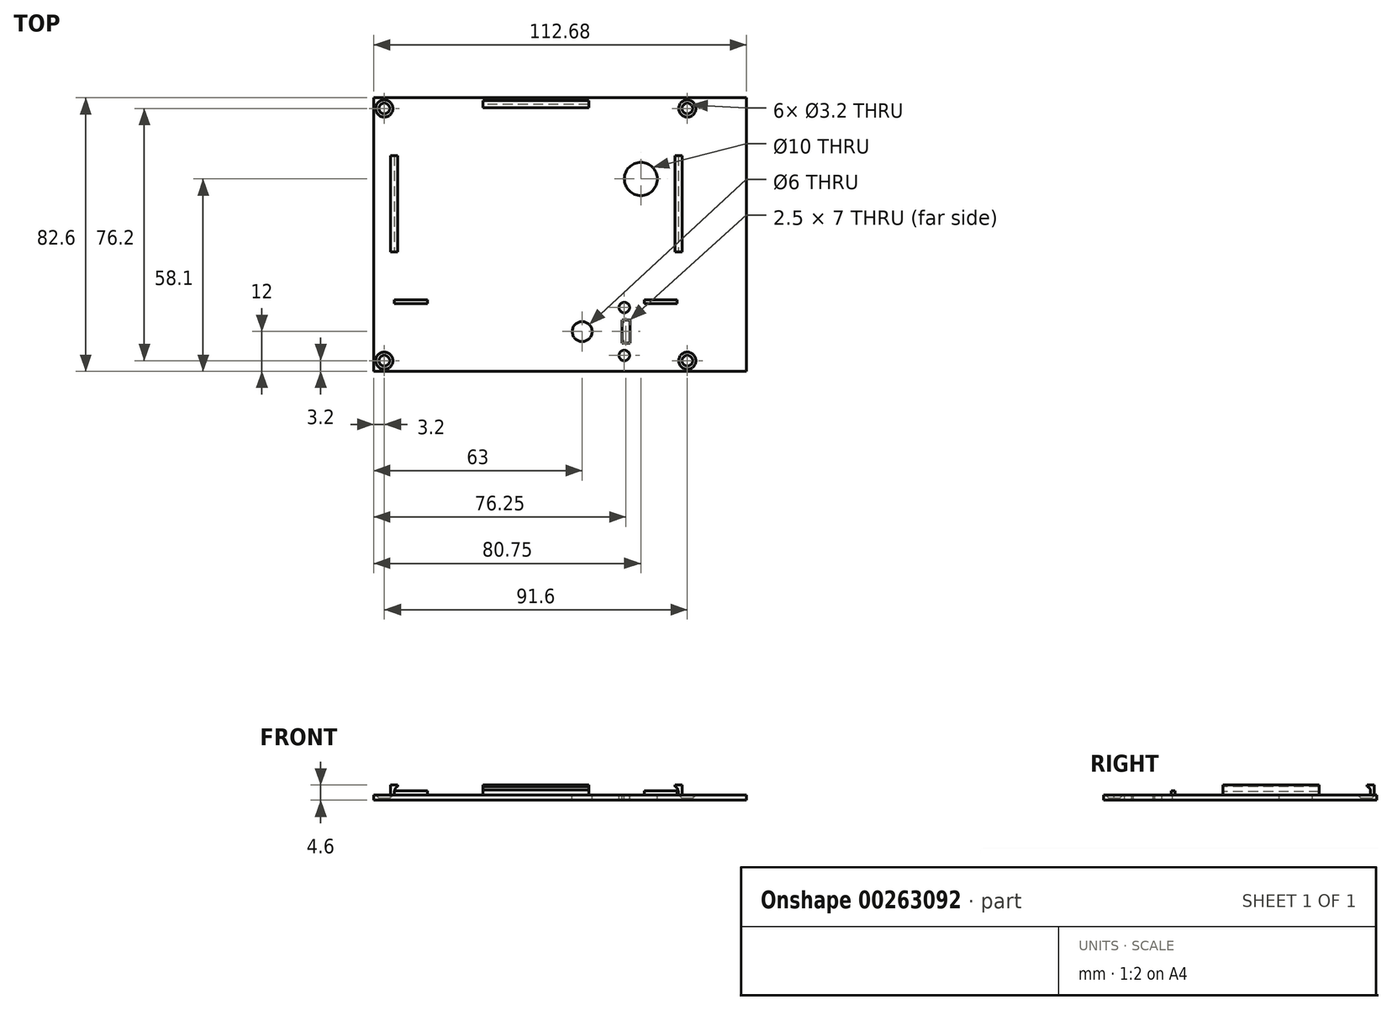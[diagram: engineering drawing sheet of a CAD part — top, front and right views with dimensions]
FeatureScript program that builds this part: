
annotation { "Feature Type Name" : "Feature", "Feature Type Description" : "" }
export const myFeature = defineFeature(function(context is Context, id is Id, definition is map)
    precondition{}
    {
        {
            var Q0;
            Q0=qCreatedBy(makeId("Top.planeOp"),FACE);
            var sketch = newSketch(context, id + "F0", { "sketchPlane" : qUnion([Q0])});
            skLineSegment(sketch, "E0.bottom", {"start": v(0, 0) * mm, "end": v(112.68, 0) * mm});
            skLineSegment(sketch, "E0.top", {"start": v(0, 82.6) * mm, "end": v(112.68, 82.6) * mm});
            skLineSegment(sketch, "E0.left", {"start": v(0, 0) * mm, "end": v(0, 82.6) * mm});
            skLineSegment(sketch, "E0.right", {"start": v(112.68, 0) * mm, "end": v(112.68, 82.6) * mm});
            skLineSegment(sketch, "E1.bottom", {"start": v(3.2, 79.4) * mm, "end": v(94.8, 79.4) * mm, "construction": true});
            skLineSegment(sketch, "E1.top", {"start": v(3.2, 3.2) * mm, "end": v(94.8, 3.2) * mm, "construction": true});
            skLineSegment(sketch, "E1.left", {"start": v(3.2, 79.4) * mm, "end": v(3.2, 3.2) * mm, "construction": true});
            skLineSegment(sketch, "E1.right", {"start": v(94.8, 79.4) * mm, "end": v(94.8, 3.2) * mm, "construction": true});
            skCircle(sketch, "E2", {"center": v(3.2, 79.4) * mm, "radius": 1.6 * mm});
            skCircle(sketch, "E3", {"center": v(94.8, 79.4) * mm, "radius": 1.6 * mm});
            skCircle(sketch, "E4", {"center": v(94.8, 3.2) * mm, "radius": 1.6 * mm});
            skCircle(sketch, "E5", {"center": v(3.2, 3.2) * mm, "radius": 1.6 * mm});
            skSolve(sketch);
        }
        {
            var Q0;
            Q0=makeQuery(id+"F0.imprint","IMPRINT",FACE,{"disambiguationData":[TD([[makeQuery(id+"F0.imprint","IMPRINT",EDGE,{"derivedFrom":sQuery(id+"F0.wireOp",EDGE,"E0.bottom")}),1.0]])]});
            var sketch = newSketch(context, id + "F1", { "sketchPlane" : qUnion([Q0])});
            skLineSegment(sketch, "E6.bottom", {"start": v(6.25, 80.6) * mm, "end": v(91.75, 80.6) * mm, "construction": true});
            skLineSegment(sketch, "E6.top", {"start": v(6.25, 21.6) * mm, "end": v(91.75, 21.6) * mm, "construction": true});
            skLineSegment(sketch, "E6.left", {"start": v(6.25, 80.6) * mm, "end": v(6.25, 21.6) * mm, "construction": true});
            skLineSegment(sketch, "E6.right", {"start": v(91.75, 80.6) * mm, "end": v(91.75, 21.6) * mm, "construction": true});
            skCircle(sketch, "E7", {"center": v(80.75, 58.1) * mm, "radius": 5 * mm});
            skLineSegment(sketch, "E8", {"start": v(49, 80.6) * mm, "end": v(49, 21.6) * mm, "construction": true});
            skLineSegment(sketch, "E9.bottom", {"start": v(6.25, 21.6) * mm, "end": v(16.25, 21.6) * mm});
            skLineSegment(sketch, "E9.top", {"start": v(6.25, 20.4) * mm, "end": v(16.25, 20.4) * mm});
            skLineSegment(sketch, "E9.left", {"start": v(6.25, 21.6) * mm, "end": v(6.25, 20.4) * mm});
            skLineSegment(sketch, "E9.right", {"start": v(16.25, 21.6) * mm, "end": v(16.25, 20.4) * mm});
            skLineSegment(sketch, "E10.bottom", {"start": v(91.75, 21.6) * mm, "end": v(81.75, 21.6) * mm});
            skLineSegment(sketch, "E10.top", {"start": v(91.75, 20.4) * mm, "end": v(81.75, 20.4) * mm});
            skLineSegment(sketch, "E10.left", {"start": v(91.75, 21.6) * mm, "end": v(91.75, 20.4) * mm});
            skLineSegment(sketch, "E10.right", {"start": v(81.75, 21.6) * mm, "end": v(81.75, 20.4) * mm});
            skSolve(sketch);
        }
        {
            var Q0;
            Q0=makeQuery(id+"F0.imprint","IMPRINT",FACE,{"disambiguationData":[TD([[makeQuery(id+"F0.imprint","IMPRINT",EDGE,{"derivedFrom":sQuery(id+"F0.wireOp",EDGE,"E0.bottom")}),1.0]])]});
            var sketch = newSketch(context, id + "F2", { "sketchPlane" : qUnion([Q0])});
            skLineSegment(sketch, "E11.bottom", {"start": v(53.5, 22.5) * mm, "end": v(82.5, 22.5) * mm, "construction": true});
            skLineSegment(sketch, "E11.top", {"start": v(53.5, 1.5) * mm, "end": v(82.5, 1.5) * mm, "construction": true});
            skLineSegment(sketch, "E11.left", {"start": v(53.5, 22.5) * mm, "end": v(53.5, 1.5) * mm, "construction": true});
            skLineSegment(sketch, "E11.right", {"start": v(82.5, 22.5) * mm, "end": v(82.5, 1.5) * mm, "construction": true});
            skCircle(sketch, "E12", {"center": v(75.75, 19.25) * mm, "radius": 1.6 * mm});
            skCircle(sketch, "E13", {"center": v(75.75, 4.75) * mm, "radius": 1.6 * mm});
            skCircle(sketch, "E14", {"center": v(63, 12) * mm, "radius": 3 * mm});
            skLineSegment(sketch, "E15.bottom", {"start": v(75, 15.5) * mm, "end": v(77.5, 15.5) * mm});
            skLineSegment(sketch, "E15.top", {"start": v(75, 8.5) * mm, "end": v(77.5, 8.5) * mm});
            skLineSegment(sketch, "E15.left", {"start": v(75, 15.5) * mm, "end": v(75, 8.5) * mm});
            skLineSegment(sketch, "E15.right", {"start": v(77.5, 15.5) * mm, "end": v(77.5, 8.5) * mm});
            skSolve(sketch);
        }
        {
            var Q0;
            Q0=makeQuery(id+"F0.imprint","IMPRINT",FACE,{"disambiguationData":[TD([[makeQuery(id+"F0.imprint","IMPRINT",EDGE,{"derivedFrom":sQuery(id+"F0.wireOp",EDGE,"E0.bottom")}),1.0]])]});
            extrude(context, id + "F3", {"entities" : qUnion([Q0]), "oppositeDirection" : true, "depth" : 1.6 * mm});
        }
        {
            var Q0;
            Q0=makeQuery(id+"F1.imprint","IMPRINT",FACE,{"disambiguationData":[TD([[makeQuery(id+"F1.imprint","IMPRINT",EDGE,{"derivedFrom":sQuery(id+"F1.wireOp",EDGE,"E7")}),1.0]])]});
            extrude(context, id + "F4", {"entities" : qUnion([Q0]), "operationType" : NewBodyOperationType.REMOVE, "endBound" : BoundingType.THROUGH_ALL, "oppositeDirection" : true, "depth" : 25 * mm});
        }
        {
            var Q0;
            Q0=makeQuery(id+"F2.imprint","IMPRINT",FACE,{"disambiguationData":[TD([[makeQuery(id+"F2.imprint","IMPRINT",EDGE,{"derivedFrom":sQuery(id+"F2.wireOp",EDGE,"E13")}),1.0]])]});
            var Q1;
            Q1=makeQuery(id+"F2.imprint","IMPRINT",FACE,{"disambiguationData":[TD([[makeQuery(id+"F2.imprint","IMPRINT",EDGE,{"derivedFrom":sQuery(id+"F2.wireOp",EDGE,"E14")}),1.0]])]});
            var Q2;
            Q2=makeQuery(id+"F2.imprint","IMPRINT",FACE,{"disambiguationData":[TD([[makeQuery(id+"F2.imprint","IMPRINT",EDGE,{"derivedFrom":sQuery(id+"F2.wireOp",EDGE,"E15.bottom")}),-1.0]])]});
            var Q3;
            Q3=makeQuery(id+"F2.imprint","IMPRINT",FACE,{"disambiguationData":[TD([[makeQuery(id+"F2.imprint","IMPRINT",EDGE,{"derivedFrom":sQuery(id+"F2.wireOp",EDGE,"E12")}),1.0]])]});
            extrude(context, id + "F5", {"entities" : qUnion([Q0, Q1, Q2, Q3]), "operationType" : NewBodyOperationType.REMOVE, "endBound" : BoundingType.THROUGH_ALL, "oppositeDirection" : true, "depth" : 25 * mm});
        }
        {
            var Q0;
            Q0=qCreatedBy(makeId("Front.planeOp"),FACE);
            var sketch = newSketch(context, id + "F6", { "sketchPlane" : qUnion([Q0])});
            skLineSegment(sketch, "E16", {"start": v(6.25, 0) * mm, "end": v(5.05, 0) * mm});
            skLineSegment(sketch, "E17.bottom", {"start": v(5.05, 0) * mm, "end": v(6.25, 0) * mm});
            skLineSegment(sketch, "E17.top", {"start": v(5.05, 0) * mm, "end": v(6.25, 0) * mm});
            skLineSegment(sketch, "E17.left", {"start": v(5.05, 0) * mm, "end": v(5.05, 0) * mm});
            skLineSegment(sketch, "E17.right", {"start": v(6.25, 0) * mm, "end": v(6.25, 0) * mm});
            skLineSegment(sketch, "E18.bottom", {"start": v(6.25, 3) * mm, "end": v(5.05, 3) * mm});
            skLineSegment(sketch, "E18.left", {"start": v(6.25, 3) * mm, "end": v(6.25, 0) * mm});
            skLineSegment(sketch, "E18.right", {"start": v(5.05, 3) * mm, "end": v(5.05, 0) * mm});
            skLineSegment(sketch, "E19", {"start": v(6.25, 3) * mm, "end": v(7.25, 3) * mm});
            skLineSegment(sketch, "E20", {"start": v(7.25, 3) * mm, "end": v(7.25, 2.5) * mm});
            skFitSpline(sketch, "E21", {"points": [v(7.25, 2.5) * mm, v(6.25, 0) * mm], "startDerivative": vector(-3.78, -0.96) * mm, "endDerivative": vector(0, -0.48) * mm});
            skLineSegment(sketch, "E22", {"start": v(49.15, 0) * mm, "end": v(49.15, 10.87) * mm, "construction": true});
            skLineSegment(sketch, "E23.MirrorCS", {"start": v(92.05, 3) * mm, "end": v(93.25, 3) * mm});
            skLineSegment(sketch, "E24.MirrorCS", {"start": v(92.05, 3) * mm, "end": v(91.05, 3) * mm});
            skLineSegment(sketch, "E25.MirrorCS", {"start": v(91.05, 3) * mm, "end": v(91.05, 2.5) * mm});
            skLineSegment(sketch, "E26.MirrorCS", {"start": v(92.05, 3) * mm, "end": v(92.05, 0) * mm});
            skFitSpline(sketch, "E27.MirrorCS", {"points": [v(91.05, 2.5) * mm, v(92.05, 0) * mm], "startDerivative": vector(3.78, -0.96) * mm, "endDerivative": vector(0, -0.48) * mm});
            skLineSegment(sketch, "E28.MirrorCS", {"start": v(92.05, 0) * mm, "end": v(93.25, 0) * mm});
            skLineSegment(sketch, "E29.MirrorCS", {"start": v(93.25, 3) * mm, "end": v(93.25, 0) * mm});
            skSolve(sketch);
        }
        {
            var Q0;
            Q0=qSketchRegion(id+"F6",true);
            extrude(context, id + "F7", {"entities" : qUnion([Q0]), "operationType" : NewBodyOperationType.ADD, "oppositeDirection" : true, "depth" : 65.1 * mm, "hasSecondDirection" : true, "secondDirectionOppositeDirection" : true, "secondDirectionDepth" : 36.1 * mm});
        }
        {
            var Q0;
            Q0=qCreatedBy(makeId("Right.planeOp"),FACE);
            var sketch = newSketch(context, id + "F8", { "sketchPlane" : qUnion([Q0])});
            skLineSegment(sketch, "E30.bottom", {"start": v(80.62, 0) * mm, "end": v(81.82, 0) * mm});
            skLineSegment(sketch, "E30.top", {"start": v(80.62, 3) * mm, "end": v(81.82, 3) * mm});
            skLineSegment(sketch, "E30.left", {"start": v(80.62, 0) * mm, "end": v(80.62, 3) * mm});
            skLineSegment(sketch, "E30.right", {"start": v(81.82, 0) * mm, "end": v(81.82, 3) * mm});
            skLineSegment(sketch, "E31", {"start": v(80.62, 3) * mm, "end": v(79.62, 3) * mm});
            skLineSegment(sketch, "E32", {"start": v(79.62, 3) * mm, "end": v(79.62, 2.5) * mm});
            skFitSpline(sketch, "E33", {"points": [v(79.62, 2.5) * mm, v(80.62, 1.5) * mm, v(80.62, 0) * mm], "startDerivative": vector(3.74, -1.12) * mm, "endDerivative": vector(0, -1.77) * mm});
            skSolve(sketch);
        }
        {
            var Q0;
            Q0=qSketchRegion(id+"F8",true);
            extrude(context, id + "F9", {"entities" : qUnion([Q0]), "operationType" : NewBodyOperationType.ADD, "depth" : 65 * mm, "hasSecondDirection" : true, "secondDirectionOppositeDirection" : false, "secondDirectionDepth" : 33 * mm});
        }
        {
            var Q0;
            Q0=makeQuery(id+"F1.imprint","IMPRINT",FACE,{"disambiguationData":[TD([[makeQuery(id+"F1.imprint","IMPRINT",EDGE,{"derivedFrom":sQuery(id+"F1.wireOp",EDGE,"E9.bottom")}),-1.0]])]});
            var Q1;
            Q1=makeQuery(id+"F1.imprint","IMPRINT",FACE,{"disambiguationData":[TD([[makeQuery(id+"F1.imprint","IMPRINT",EDGE,{"derivedFrom":sQuery(id+"F1.wireOp",EDGE,"E10.bottom")}),1.0]])]});
            extrude(context, id + "F10", {"entities" : qUnion([Q0, Q1]), "operationType" : NewBodyOperationType.ADD, "depth" : 1.2 * mm});
        }
        {
            var Q0;
            Q0=makeQuery(id+"F3.opExtrude","CAP_EDGE",EDGE,{"disambiguationData":[OSD([sQuery(id+"F0.wireOp",EDGE,"E2")])],"isStart":true});
            var Q1;
            Q1=makeQuery(id+"F3.opExtrude","CAP_EDGE",EDGE,{"disambiguationData":[OSD([sQuery(id+"F0.wireOp",EDGE,"E5")])],"isStart":true});
            var Q2;
            Q2=makeQuery(id+"F5.boolean.opBoolean","COPY",EDGE,{"derivedFrom":makeQuery(id+"F5.opExtrude","CAP_EDGE",EDGE,{"disambiguationData":[OSD([sQuery(id+"F2.wireOp",EDGE,"E13")])],"isStart":true})});
            var Q3;
            Q3=makeQuery(id+"F5.boolean.opBoolean","COPY",EDGE,{"derivedFrom":makeQuery(id+"F5.opExtrude","CAP_EDGE",EDGE,{"disambiguationData":[OSD([sQuery(id+"F2.wireOp",EDGE,"E12")])],"isStart":true})});
            var Q4;
            Q4=makeQuery(id+"F3.opExtrude","CAP_EDGE",EDGE,{"disambiguationData":[OSD([sQuery(id+"F0.wireOp",EDGE,"E4")])],"isStart":true});
            var Q5;
            Q5=makeQuery(id+"F3.opExtrude","CAP_EDGE",EDGE,{"disambiguationData":[OSD([sQuery(id+"F0.wireOp",EDGE,"E3")])],"isStart":true});
            chamfer(context, id + "F11", {"entities" : qUnion([Q0, Q1, Q2, Q3, Q4, Q5]), "width" : 1 * mm, "tangentPropagation" : true});
        }
    });
